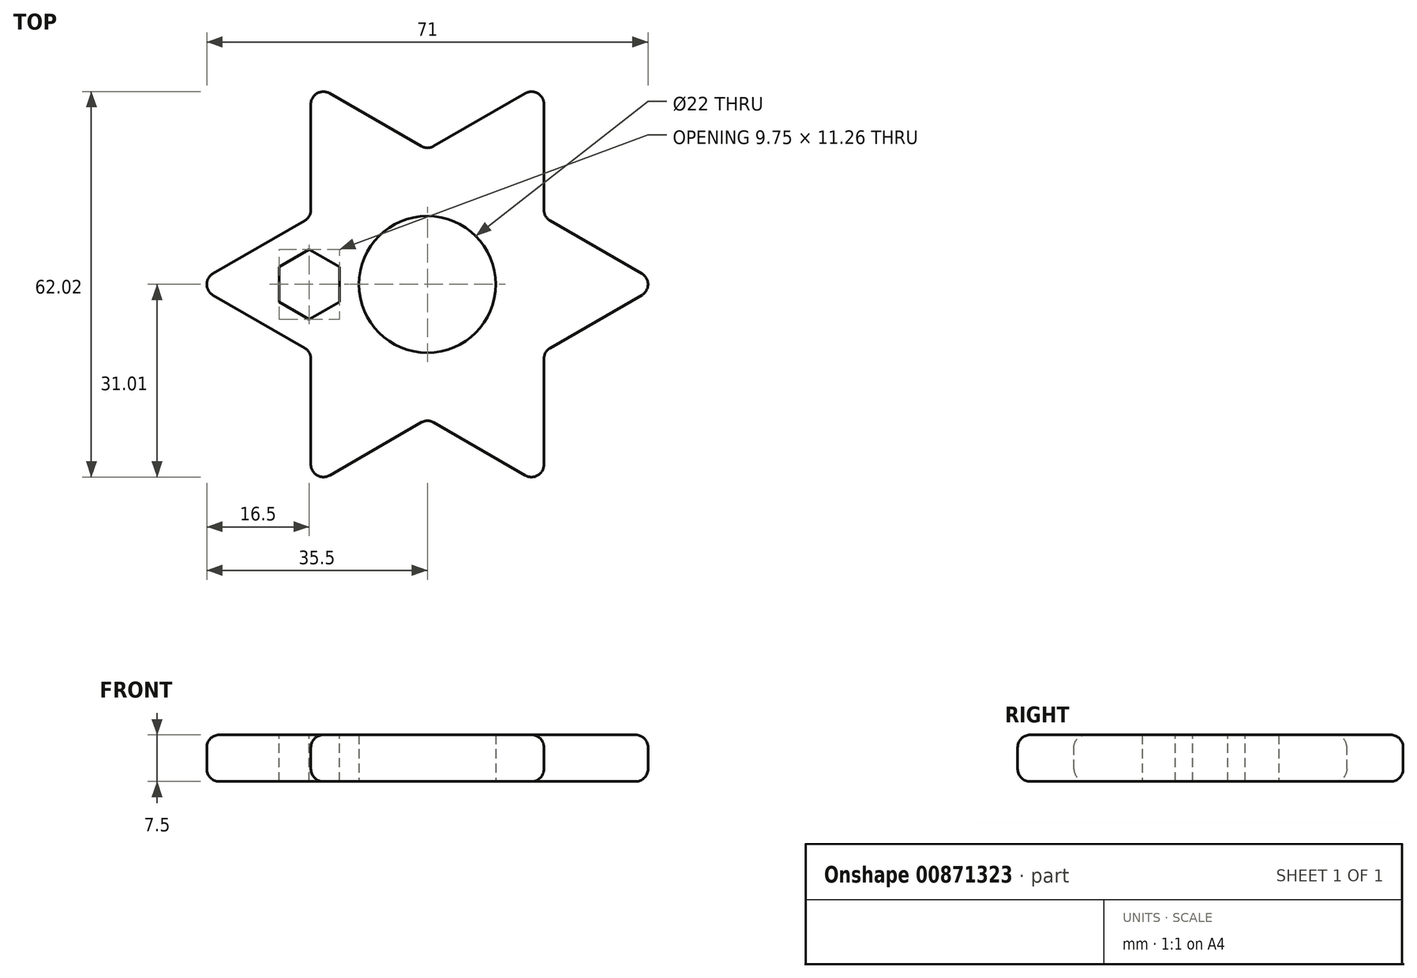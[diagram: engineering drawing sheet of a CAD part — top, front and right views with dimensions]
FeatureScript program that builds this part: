
annotation { "Feature Type Name" : "Feature", "Feature Type Description" : "" }
export const myFeature = defineFeature(function(context is Context, id is Id, definition is map)
    precondition{}
    {
        {
            var Q0;
            Q0=qCreatedBy(makeId("Top.planeOp"),FACE);
            var sketch = newSketch(context, id + "F0", { "sketchPlane" : qUnion([Q0])});
            skCircle(sketch, "E0", {"center": v(0, 0) * mm, "radius": 37.5 * mm, "construction": true});
            skCircle(sketch, "E1", {"center": v(37.5, 0) * mm, "radius": 37.5 * mm, "construction": true});
            skCircle(sketch, "E2", {"center": v(18.75, 32.48) * mm, "radius": 37.5 * mm, "construction": true});
            skCircle(sketch, "E3", {"center": v(-18.75, 32.48) * mm, "radius": 37.5 * mm, "construction": true});
            skCircle(sketch, "E4", {"center": v(-37.5, 0) * mm, "radius": 37.5 * mm, "construction": true});
            skLineSegment(sketch, "E5", {"start": v(-37.5, 0) * mm, "end": v(-18.75, -32.48) * mm, "construction": true});
            skLineSegment(sketch, "E6", {"start": v(-18.75, -32.48) * mm, "end": v(18.75, -32.48) * mm, "construction": true});
            skLineSegment(sketch, "E7", {"start": v(18.75, -32.48) * mm, "end": v(37.5, 0) * mm, "construction": true});
            skLineSegment(sketch, "E8", {"start": v(37.5, 0) * mm, "end": v(18.75, 32.48) * mm, "construction": true});
            skLineSegment(sketch, "E9", {"start": v(-18.75, 32.48) * mm, "end": v(18.75, 32.48) * mm, "construction": true});
            skLineSegment(sketch, "E10", {"start": v(-37.5, 0) * mm, "end": v(-18.75, 32.48) * mm, "construction": true});
            skLineSegment(sketch, "E11", {"start": v(-18.75, 32.48) * mm, "end": v(-18.75, -32.48) * mm});
            skLineSegment(sketch, "E12", {"start": v(-18.75, 32.48) * mm, "end": v(37.5, 0) * mm});
            skLineSegment(sketch, "E13", {"start": v(37.5, 0) * mm, "end": v(-18.75, -32.48) * mm});
            skLineSegment(sketch, "E14", {"start": v(18.75, 32.48) * mm, "end": v(18.75, -32.48) * mm});
            skLineSegment(sketch, "E15", {"start": v(18.75, -32.48) * mm, "end": v(-37.5, 0) * mm});
            skLineSegment(sketch, "E16", {"start": v(-37.5, 0) * mm, "end": v(18.75, 32.48) * mm});
            skCircle(sketch, "E17", {"center": v(0, 0) * mm, "radius": 11 * mm});
            skSolve(sketch);
        }
        {
            var Q0;
            Q0 = qSketchRegion(id + "F0", true);
            extrude(context, id + "F1", {"entities" : qUnion([Q0]), "depth" : 7.5 * mm, "offsetDistance" : 25 * mm});
        }
        {
            var Q0;
            Q0=makeQuery(id+"F1.opExtrude","SWEPT_EDGE",EDGE,{"disambiguationData":[OSD([sQuery(id+"F0.wireOp",EDGE,"E11"),sQuery(id+"F0.wireOp",EDGE,"E13")])]});
            var Q1;
            Q1=makeQuery(id+"F1.opExtrude","SWEPT_EDGE",EDGE,{"disambiguationData":[OSD([sQuery(id+"F0.wireOp",EDGE,"E13"),sQuery(id+"F0.wireOp",EDGE,"E15")])]});
            var Q2;
            Q2=makeQuery(id+"F1.opExtrude","SWEPT_EDGE",EDGE,{"disambiguationData":[OSD([sQuery(id+"F0.wireOp",EDGE,"E14"),sQuery(id+"F0.wireOp",EDGE,"E15")])]});
            var Q3;
            Q3=makeQuery(id+"F1.opExtrude","SWEPT_EDGE",EDGE,{"disambiguationData":[OSD([sQuery(id+"F0.wireOp",EDGE,"E13"),sQuery(id+"F0.wireOp",EDGE,"E14")])]});
            var Q4;
            Q4=makeQuery(id+"F1.opExtrude","SWEPT_EDGE",EDGE,{"disambiguationData":[OSD([sQuery(id+"F0.wireOp",EDGE,"E12"),sQuery(id+"F0.wireOp",EDGE,"E13")])]});
            var Q5;
            Q5=makeQuery(id+"F1.opExtrude","SWEPT_EDGE",EDGE,{"disambiguationData":[OSD([sQuery(id+"F0.wireOp",EDGE,"E12"),sQuery(id+"F0.wireOp",EDGE,"E14")])]});
            var Q6;
            Q6=makeQuery(id+"F1.opExtrude","SWEPT_EDGE",EDGE,{"disambiguationData":[OSD([sQuery(id+"F0.wireOp",EDGE,"E14"),sQuery(id+"F0.wireOp",EDGE,"E16")])]});
            var Q7;
            Q7=makeQuery(id+"F1.opExtrude","SWEPT_EDGE",EDGE,{"disambiguationData":[OSD([sQuery(id+"F0.wireOp",EDGE,"E12"),sQuery(id+"F0.wireOp",EDGE,"E16")])]});
            var Q8;
            Q8=makeQuery(id+"F1.opExtrude","SWEPT_EDGE",EDGE,{"disambiguationData":[OSD([sQuery(id+"F0.wireOp",EDGE,"E11"),sQuery(id+"F0.wireOp",EDGE,"E12")])]});
            var Q9;
            Q9=makeQuery(id+"F1.opExtrude","SWEPT_EDGE",EDGE,{"disambiguationData":[OSD([sQuery(id+"F0.wireOp",EDGE,"E15"),sQuery(id+"F0.wireOp",EDGE,"E16")])]});
            var Q10;
            Q10=makeQuery(id+"F1.opExtrude","SWEPT_EDGE",EDGE,{"disambiguationData":[OSD([sQuery(id+"F0.wireOp",EDGE,"E11"),sQuery(id+"F0.wireOp",EDGE,"E15")])]});
            var Q11;
            Q11=makeQuery(id+"F1.opExtrude","SWEPT_EDGE",EDGE,{"disambiguationData":[OSD([sQuery(id+"F0.wireOp",EDGE,"E11"),sQuery(id+"F0.wireOp",EDGE,"E16")])]});
            fillet(context, id + "F2", {"entities" : qUnion([Q0, Q1, Q2, Q3, Q4, Q5, Q6, Q7, Q8, Q9, Q10, Q11]), "radius" : 2 * mm, "tangentPropagation" : true, "allowEdgeOverflow" : false});
        }
        {
            var Q0;
            {var subQ0=sQuery(id+"F0.wireOp",EDGE,"E13");Q0=makeQuery(id+"F1.opExtrude","CAP_EDGE",EDGE,{"disambiguationData":[OSD([subQ0]),TDD([makeQuery(id+"F0.imprint","IMPRINT",EDGE,{"disambiguationData":[TD([[makeQuery(id+"F0.imprint","INTERSECT",VERTEX,{"derivedFrom":[sQuery(id+"F0.wireOp",EDGE,"E11"),subQ0]}),1.0]])],"derivedFrom":subQ0})])],"isStart":true});}
            var Q1;
            {var subQ0=sQuery(id+"F0.wireOp",EDGE,"E13");Q1=makeQuery(id+"F1.opExtrude","CAP_EDGE",EDGE,{"disambiguationData":[OSD([subQ0]),TDD([makeQuery(id+"F0.imprint","IMPRINT",EDGE,{"disambiguationData":[TD([[makeQuery(id+"F0.imprint","INTERSECT",VERTEX,{"derivedFrom":[sQuery(id+"F0.wireOp",EDGE,"E11"),subQ0]}),1.0]])],"derivedFrom":subQ0})])],"isStart":false});}
            fillet(context, id + "F3", {"entities" : qUnion([Q0, Q1]), "radius" : 2 * mm, "tangentPropagation" : true, "allowEdgeOverflow" : false});
        }
        {
            var Q0;
            Q0=makeQuery(id+"F1.opExtrude","CAP_FACE",FACE,{"disambiguationData":[OSD([sQuery(id+"F0.wireOp",EDGE,"E11"),sQuery(id+"F0.wireOp",EDGE,"E12"),sQuery(id+"F0.wireOp",EDGE,"E13"),sQuery(id+"F0.wireOp",EDGE,"E14"),sQuery(id+"F0.wireOp",EDGE,"E15"),sQuery(id+"F0.wireOp",EDGE,"E16"),sQuery(id+"F0.wireOp",EDGE,"E17")])],"isStart":false});
            var sketch = newSketch(context, id + "F4", { "sketchPlane" : qUnion([Q0])});
            skCircle(sketch, "E18.cCircle", {"center": v(-19, 0) * mm, "radius": 4.88 * mm, "construction": true});
            skLineSegment(sketch, "E18.0", {"start": v(-14.12, 2.81) * mm, "end": v(-14.12, -2.81) * mm});
            skLineSegment(sketch, "E18.1", {"start": v(-14.12, -2.81) * mm, "end": v(-19, -5.63) * mm});
            skLineSegment(sketch, "E18.2", {"start": v(-19, -5.63) * mm, "end": v(-23.88, -2.81) * mm});
            skLineSegment(sketch, "E18.3", {"start": v(-23.88, -2.81) * mm, "end": v(-23.88, 2.81) * mm});
            skLineSegment(sketch, "E18.4", {"start": v(-23.88, 2.81) * mm, "end": v(-19, 5.63) * mm});
            skLineSegment(sketch, "E18.5", {"start": v(-19, 5.63) * mm, "end": v(-14.12, 2.81) * mm});
            skPoint(sketch, "E18.0.midPoint", {"position": v(-14.12, 0) * mm});
            skSolve(sketch);
        }
        {
            var Q0;
            Q0=makeQuery(id+"F4.imprint","IMPRINT",FACE,{"disambiguationData":[TD([[makeQuery(id+"F4.imprint","IMPRINT",EDGE,{"derivedFrom":sQuery(id+"F4.wireOp",EDGE,"E18.0")}),-1.0]])]});
            extrude(context, id + "F5", {"entities" : qUnion([Q0]), "operationType" : NewBodyOperationType.REMOVE, "oppositeDirection" : true, "depth" : 25 * mm, "offsetDistance" : 25 * mm});
        }
    });
